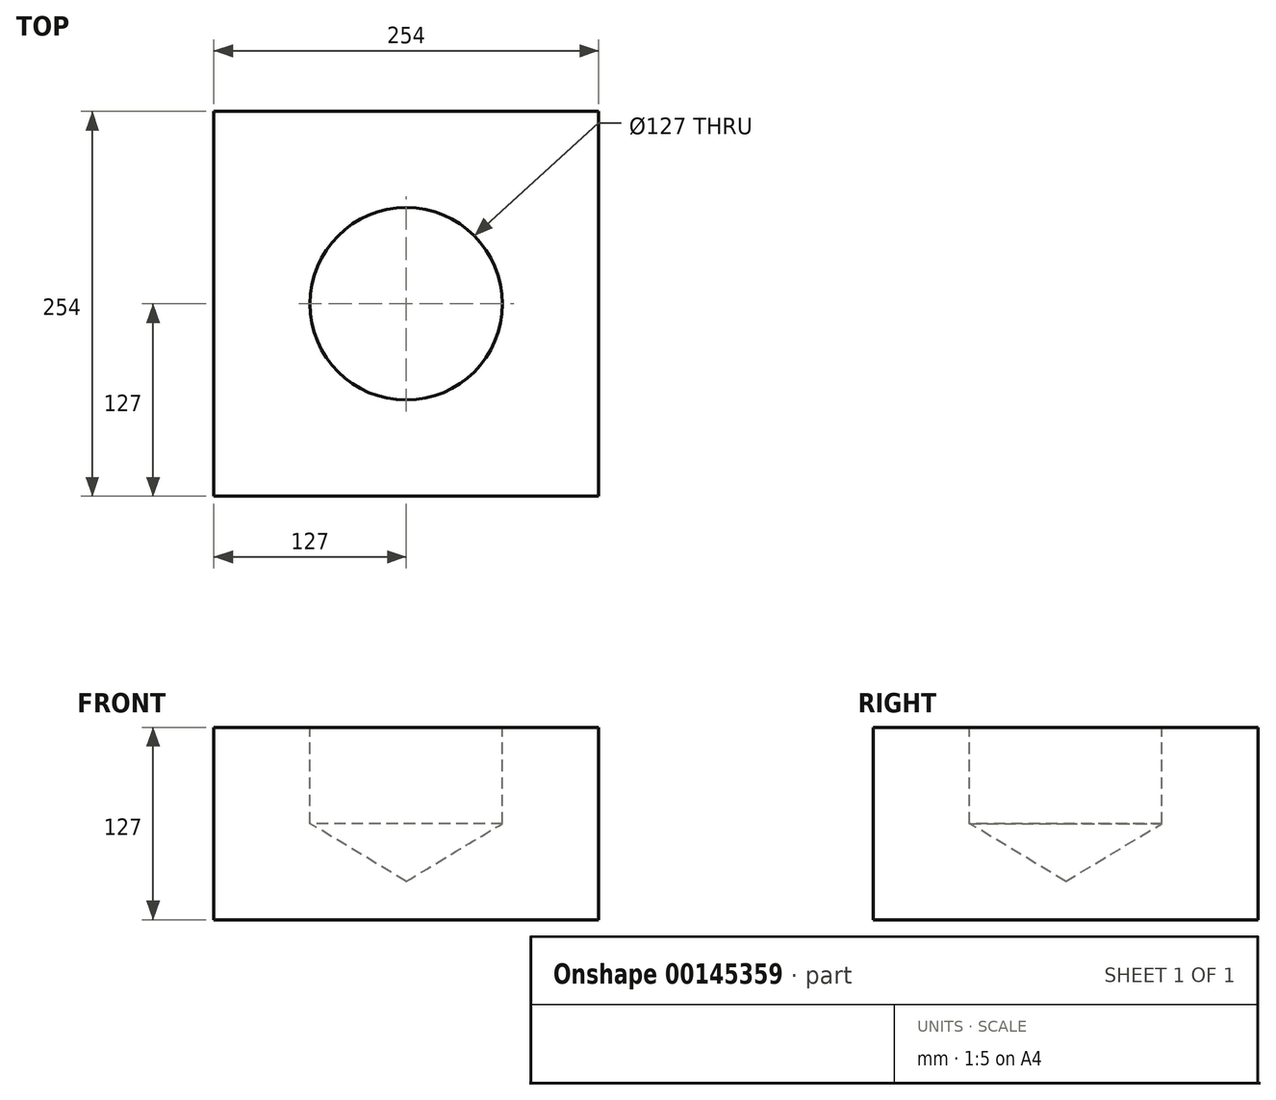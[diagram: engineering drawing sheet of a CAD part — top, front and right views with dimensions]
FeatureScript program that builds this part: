
annotation { "Feature Type Name" : "Feature", "Feature Type Description" : "" }
export const myFeature = defineFeature(function(context is Context, id is Id, definition is map)
    precondition{}
    {
        {
            var Q0;
            Q0=qCreatedBy(makeId("Top.planeOp"),FACE);
            var sketch = newSketch(context, id + "F0", { "sketchPlane" : qUnion([Q0])});
            skLineSegment(sketch, "E0.bottom", {"start": v(-127, 127) * mm, "end": v(127, 127) * mm});
            skLineSegment(sketch, "E0.top", {"start": v(-127, -127) * mm, "end": v(127, -127) * mm});
            skLineSegment(sketch, "E0.left", {"start": v(-127, 127) * mm, "end": v(-127, -127) * mm});
            skLineSegment(sketch, "E0.right", {"start": v(127, 127) * mm, "end": v(127, -127) * mm});
            skPoint(sketch, "E0.middle", {"position": v(0, 0) * mm});
            skSolve(sketch);
        }
        {
            var Q0;
            Q0 = qSketchRegion(id + "F0", true);
            extrude(context, id + "F1", {"entities" : qUnion([Q0]), "depth" : 127 * mm});
        }
        {
            var Q0;
            Q0=makeQuery(id+"F1.opExtrude","CAP_FACE",FACE,{"disambiguationData":[OSD([sQuery(id+"F0.wireOp",EDGE,"E0.bottom"),sQuery(id+"F0.wireOp",EDGE,"E0.top"),sQuery(id+"F0.wireOp",EDGE,"E0.left"),sQuery(id+"F0.wireOp",EDGE,"E0.right")])],"isStart":false});
            var sketch = newSketch(context, id + "F2", { "sketchPlane" : qUnion([Q0])});
            skCircle(sketch, "E1", {"center": v(0, 0) * mm, "radius": 74.67 * mm});
            skSolve(sketch);
        }
        {
            var Q0;
            Q0=makeQuery(id+"F2.imprint","IMPRINT",FACE,{"disambiguationData":[TD([[makeQuery(id+"F2.imprint","IMPRINT",EDGE,{"derivedFrom":sQuery(id+"F2.wireOp",EDGE,"E1")}),1.0]])]});
            var sketch = newSketch(context, id + "F3", { "sketchPlane" : qUnion([Q0])});
            skPoint(sketch, "E2", {"position": v(0, 0) * mm});
            skSolve(sketch);
        }
        {
            var Q0;
            Q0=sQuery(id+"F3.wireOp",VERTEX,"E2");
            var Q1;
            Q1=makeQuery(id+"F1.opExtrude","SWEPT_BODY",BODY,{"disambiguationData":[OSD([sQuery(id+"F0.wireOp",EDGE,"E0.bottom"),sQuery(id+"F0.wireOp",EDGE,"E0.top"),sQuery(id+"F0.wireOp",EDGE,"E0.left"),sQuery(id+"F0.wireOp",EDGE,"E0.right")])]});
            hole(context, id + "F4", {"style" : HoleStyle.SIMPLE, "endStyle" : HoleEndStyle.BLIND, "holeDiameter" : 127 * mm, "holeDepth" : 63.5 * mm, "locations" : qUnion([Q0]), "scope" : qUnion([Q1])});
        }
    });
